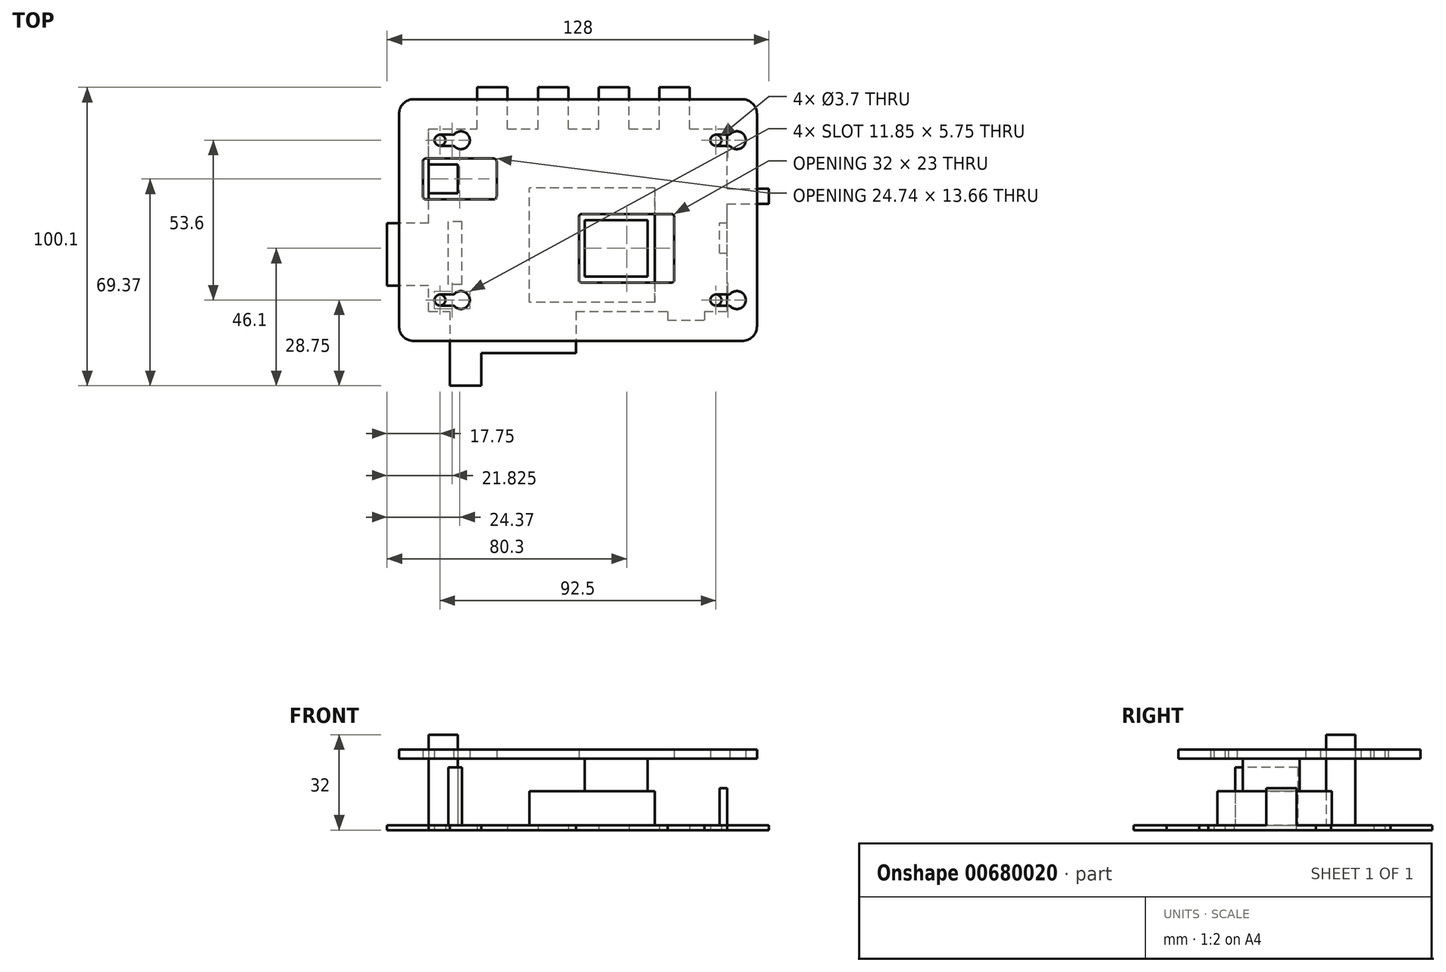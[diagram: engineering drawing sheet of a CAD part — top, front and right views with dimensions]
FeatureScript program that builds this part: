
annotation { "Feature Type Name" : "Feature", "Feature Type Description" : "" }
export const myFeature = defineFeature(function(context is Context, id is Id, definition is map)
    precondition{}
    {
        {
            var Q0;
            Q0=qCreatedBy(makeId("Top.planeOp"),FACE);
            var sketch = newSketch(context, id + "F0", { "sketchPlane" : qUnion([Q0])});
            skLineSegment(sketch, "E0.bottom", {"start": v(0, 0) * mm, "end": v(100, 0) * mm});
            skLineSegment(sketch, "E0.top", {"start": v(0, 61.1) * mm, "end": v(100, 61.1) * mm});
            skLineSegment(sketch, "E0.left", {"start": v(0, 0) * mm, "end": v(0, 61.1) * mm});
            skLineSegment(sketch, "E0.right", {"start": v(100, 0) * mm, "end": v(100, 61.1) * mm});
            skLineSegment(sketch, "E1.bottom", {"start": v(3.75, 3.75) * mm, "end": v(96.25, 3.75) * mm, "construction": true});
            skLineSegment(sketch, "E1.top", {"start": v(3.75, 57.35) * mm, "end": v(96.25, 57.35) * mm, "construction": true});
            skLineSegment(sketch, "E1.left", {"start": v(3.75, 3.75) * mm, "end": v(3.75, 57.35) * mm, "construction": true});
            skLineSegment(sketch, "E1.right", {"start": v(96.25, 3.75) * mm, "end": v(96.25, 57.35) * mm, "construction": true});
            skCircle(sketch, "E2", {"center": v(3.75, 3.75) * mm, "radius": 1.85 * mm});
            skCircle(sketch, "E3", {"center": v(3.75, 57.35) * mm, "radius": 1.85 * mm});
            skCircle(sketch, "E4", {"center": v(96.25, 57.35) * mm, "radius": 1.85 * mm});
            skCircle(sketch, "E5", {"center": v(96.25, 3.75) * mm, "radius": 1.85 * mm});
            skLineSegment(sketch, "E6.bottom", {"start": v(0, 49.2) * mm, "end": v(9.74, 49.2) * mm});
            skLineSegment(sketch, "E6.top", {"start": v(0, 39.54) * mm, "end": v(9.74, 39.54) * mm});
            skLineSegment(sketch, "E6.left", {"start": v(0, 49.2) * mm, "end": v(0, 39.54) * mm});
            skLineSegment(sketch, "E6.right", {"start": v(9.74, 49.2) * mm, "end": v(9.74, 39.54) * mm});
            skLineSegment(sketch, "E7.bottom", {"start": v(6.58, 30) * mm, "end": v(11.08, 30) * mm});
            skLineSegment(sketch, "E7.top", {"start": v(6.58, 9) * mm, "end": v(11.08, 9) * mm});
            skLineSegment(sketch, "E7.left", {"start": v(6.58, 30) * mm, "end": v(6.58, 9) * mm});
            skLineSegment(sketch, "E7.right", {"start": v(11.08, 30) * mm, "end": v(11.08, 9) * mm});
            skLineSegment(sketch, "E8.bottom", {"start": v(7.05, 0) * mm, "end": v(17.55, 0) * mm});
            skLineSegment(sketch, "E8.top", {"start": v(7.05, -25) * mm, "end": v(17.55, -25) * mm});
            skLineSegment(sketch, "E8.left", {"start": v(7.05, 0) * mm, "end": v(7.05, -25) * mm});
            skLineSegment(sketch, "E8.right", {"start": v(17.55, 0) * mm, "end": v(17.55, -25) * mm});
            skLineSegment(sketch, "E9.bottom", {"start": v(17.5, 0) * mm, "end": v(49.3, 0) * mm});
            skLineSegment(sketch, "E9.top", {"start": v(17.5, -14) * mm, "end": v(49.3, -14) * mm});
            skLineSegment(sketch, "E9.left", {"start": v(17.5, 0) * mm, "end": v(17.5, -14) * mm});
            skLineSegment(sketch, "E9.right", {"start": v(49.3, 0) * mm, "end": v(49.3, -14) * mm});
            skLineSegment(sketch, "E10.bottom", {"start": v(80.05, 0) * mm, "end": v(92.35, 0) * mm});
            skLineSegment(sketch, "E10.top", {"start": v(80.05, -3) * mm, "end": v(92.35, -3) * mm});
            skLineSegment(sketch, "E10.left", {"start": v(80.05, 0) * mm, "end": v(80.05, -3) * mm});
            skLineSegment(sketch, "E10.right", {"start": v(92.35, 0) * mm, "end": v(92.35, -3) * mm});
            skLineSegment(sketch, "E11.bottom", {"start": v(16.23, 61.1) * mm, "end": v(26.39, 61.1) * mm});
            skLineSegment(sketch, "E11.top", {"start": v(16.23, 75.1) * mm, "end": v(26.39, 75.1) * mm});
            skLineSegment(sketch, "E11.left", {"start": v(16.23, 61.1) * mm, "end": v(16.23, 75.1) * mm});
            skLineSegment(sketch, "E11.right", {"start": v(26.39, 61.1) * mm, "end": v(26.39, 75.1) * mm});
            skLineSegment(sketch, "E12.bottom", {"start": v(36.59, 61.1) * mm, "end": v(46.75, 61.1) * mm});
            skLineSegment(sketch, "E12.top", {"start": v(36.59, 75.1) * mm, "end": v(46.75, 75.1) * mm});
            skLineSegment(sketch, "E12.left", {"start": v(36.59, 61.1) * mm, "end": v(36.59, 75.1) * mm});
            skLineSegment(sketch, "E12.right", {"start": v(46.75, 61.1) * mm, "end": v(46.75, 75.1) * mm});
            skLineSegment(sketch, "E13.bottom", {"start": v(56.95, 61.1) * mm, "end": v(67.1, 61.1) * mm});
            skLineSegment(sketch, "E13.top", {"start": v(56.95, 75.1) * mm, "end": v(67.1, 75.1) * mm});
            skLineSegment(sketch, "E13.left", {"start": v(56.95, 61.1) * mm, "end": v(56.95, 75.1) * mm});
            skLineSegment(sketch, "E13.right", {"start": v(67.1, 61.1) * mm, "end": v(67.1, 75.1) * mm});
            skLineSegment(sketch, "E14.bottom", {"start": v(77.3, 61.1) * mm, "end": v(87.47, 61.1) * mm});
            skLineSegment(sketch, "E14.top", {"start": v(77.3, 75.1) * mm, "end": v(87.47, 75.1) * mm});
            skLineSegment(sketch, "E14.left", {"start": v(77.3, 61.1) * mm, "end": v(77.3, 75.1) * mm});
            skLineSegment(sketch, "E14.right", {"start": v(87.47, 61.1) * mm, "end": v(87.47, 75.1) * mm});
            skLineSegment(sketch, "E15", {"start": v(26.39, 75.1) * mm, "end": v(36.59, 75.1) * mm, "construction": true});
            skLineSegment(sketch, "E16", {"start": v(46.75, 75.1) * mm, "end": v(56.95, 75.1) * mm, "construction": true});
            skLineSegment(sketch, "E17", {"start": v(67.1, 75.1) * mm, "end": v(77.3, 75.1) * mm, "construction": true});
            skLineSegment(sketch, "E18.bottom", {"start": v(100, 29.6) * mm, "end": v(97.46, 29.6) * mm});
            skLineSegment(sketch, "E18.top", {"start": v(100, 19.44) * mm, "end": v(97.46, 19.44) * mm});
            skLineSegment(sketch, "E18.left", {"start": v(100, 29.6) * mm, "end": v(100, 19.44) * mm});
            skLineSegment(sketch, "E18.right", {"start": v(97.46, 29.6) * mm, "end": v(97.46, 19.44) * mm});
            skLineSegment(sketch, "E19.bottom", {"start": v(100, 41.1) * mm, "end": v(114, 41.1) * mm});
            skLineSegment(sketch, "E19.top", {"start": v(100, 36) * mm, "end": v(114, 36) * mm});
            skLineSegment(sketch, "E19.left", {"start": v(100, 41.1) * mm, "end": v(100, 36) * mm});
            skLineSegment(sketch, "E19.right", {"start": v(114, 41.1) * mm, "end": v(114, 36) * mm});
            skPoint(sketch, "E20", {"position": v(12.3, 0) * mm});
            skLineSegment(sketch, "E21.bottom", {"start": v(0, 29.5) * mm, "end": v(-14, 29.5) * mm});
            skLineSegment(sketch, "E21.top", {"start": v(0, 8.6) * mm, "end": v(-14, 8.6) * mm});
            skLineSegment(sketch, "E21.left", {"start": v(0, 29.5) * mm, "end": v(0, 8.6) * mm});
            skLineSegment(sketch, "E21.right", {"start": v(-14, 29.5) * mm, "end": v(-14, 8.6) * mm});
            skSolve(sketch);
        }
        {
            var Q0;
            Q0=qSketchRegion(id+"F0",true);
            var Q1;
            Q1=makeQuery(id+"F0.imprint","IMPRINT",FACE,{"disambiguationData":[TD([[makeQuery(id+"F0.imprint","IMPRINT",EDGE,{"derivedFrom":sQuery(id+"F0.wireOp",EDGE,"E7.bottom")}),-1.0]])]});
            extrude(context, id + "F1", {"entities" : qUnion([Q0, Q1]), "depth" : 1.6 * mm});
        }
        {
            var Q0;
            Q0=makeQuery(id+"F0.imprint","IMPRINT",FACE,{"disambiguationData":[TD([[makeQuery(id+"F0.imprint","IMPRINT",EDGE,{"derivedFrom":sQuery(id+"F0.wireOp",EDGE,"E6.bottom")}),-1.0]])]});
            extrude(context, id + "F2", {"entities" : qUnion([Q0]), "operationType" : NewBodyOperationType.ADD, "depth" : 32 * mm});
        }
        {
            var Q0;
            Q0=makeQuery(id+"F0.imprint","IMPRINT",FACE,{"disambiguationData":[TD([[makeQuery(id+"F0.imprint","IMPRINT",EDGE,{"derivedFrom":sQuery(id+"F0.wireOp",EDGE,"E7.bottom")}),-1.0]])]});
            extrude(context, id + "F3", {"entities" : qUnion([Q0]), "operationType" : NewBodyOperationType.ADD, "depth" : 21 * mm});
        }
        {
            var Q0;
            Q0=makeQuery(id+"F0.imprint","IMPRINT",FACE,{"disambiguationData":[TD([[makeQuery(id+"F0.imprint","IMPRINT",EDGE,{"derivedFrom":sQuery(id+"F0.wireOp",EDGE,"E18.bottom")}),1.0]])]});
            extrude(context, id + "F4", {"entities" : qUnion([Q0]), "operationType" : NewBodyOperationType.ADD, "depth" : 14 * mm});
        }
        {
            var Q0;
            Q0=qCreatedBy(makeId("Top.planeOp"),FACE);
            var sketch = newSketch(context, id + "F5", { "sketchPlane" : qUnion([Q0])});
            skLineSegment(sketch, "E22.bottom", {"start": v(33.7, 41.4) * mm, "end": v(75.8, 41.4) * mm});
            skLineSegment(sketch, "E22.top", {"start": v(33.7, 3) * mm, "end": v(75.8, 3) * mm});
            skLineSegment(sketch, "E22.left", {"start": v(33.7, 41.4) * mm, "end": v(33.7, 3) * mm});
            skLineSegment(sketch, "E22.right", {"start": v(75.8, 41.4) * mm, "end": v(75.8, 3) * mm});
            skLineSegment(sketch, "E23.bottom", {"start": v(73.3, 30.6) * mm, "end": v(52.3, 30.6) * mm});
            skLineSegment(sketch, "E23.top", {"start": v(73.3, 11.6) * mm, "end": v(52.3, 11.6) * mm});
            skLineSegment(sketch, "E23.left", {"start": v(73.3, 30.6) * mm, "end": v(73.3, 11.6) * mm});
            skLineSegment(sketch, "E23.right", {"start": v(52.3, 30.6) * mm, "end": v(52.3, 11.6) * mm});
            skPoint(sketch, "E23.middle", {"position": v(62.8, 21.1) * mm});
            skSolve(sketch);
        }
        {
            var Q0;
            Q0=makeQuery(id+"F5.imprint","IMPRINT",FACE,{"disambiguationData":[TD([[makeQuery(id+"F5.imprint","IMPRINT",EDGE,{"derivedFrom":sQuery(id+"F5.wireOp",EDGE,"E23.bottom")}),1.0]])]});
            var Q1;
            Q1=makeQuery(id+"F5.imprint","IMPRINT",FACE,{"disambiguationData":[TD([[makeQuery(id+"F5.imprint","IMPRINT",EDGE,{"derivedFrom":sQuery(id+"F5.wireOp",EDGE,"E22.bottom")}),-1.0]])]});
            extrude(context, id + "F6", {"entities" : qUnion([Q0, Q1]), "operationType" : NewBodyOperationType.ADD, "depth" : 13 * mm});
        }
        {
            var Q0;
            Q0=makeQuery(id+"F5.imprint","IMPRINT",FACE,{"disambiguationData":[TD([[makeQuery(id+"F5.imprint","IMPRINT",EDGE,{"derivedFrom":sQuery(id+"F5.wireOp",EDGE,"E23.bottom")}),1.0]])]});
            extrude(context, id + "F7", {"entities" : qUnion([Q0]), "operationType" : NewBodyOperationType.ADD, "depth" : 24 * mm});
        }
        {
            var Q0;
            Q0=makeQuery(id+"F7.opExtrude","CAP_FACE",FACE,{"disambiguationData":[OSD([sQuery(id+"F5.wireOp",EDGE,"E23.bottom"),sQuery(id+"F5.wireOp",EDGE,"E23.top"),sQuery(id+"F5.wireOp",EDGE,"E23.left"),sQuery(id+"F5.wireOp",EDGE,"E23.right")])],"isStart":false});
            var sketch = newSketch(context, id + "F8", { "sketchPlane" : qUnion([Q0])});
            skCircle(sketch, "E24.0", {"center": v(96.25, 57.35) * mm, "radius": 1.85 * mm});
            skCircle(sketch, "E25.0", {"center": v(96.25, 3.75) * mm, "radius": 1.85 * mm});
            skCircle(sketch, "E26.0", {"center": v(3.75, 3.75) * mm, "radius": 1.85 * mm});
            skCircle(sketch, "E27.0", {"center": v(3.75, 57.35) * mm, "radius": 1.85 * mm});
            skPoint(sketch, "E28.0", {"position": v(0, 61.1) * mm});
            skPoint(sketch, "E29.0", {"position": v(100, 61.1) * mm});
            skPoint(sketch, "E30.0", {"position": v(100, 0) * mm});
            skLineSegment(sketch, "E31.0.0", {"start": v(52.3, 11.6) * mm, "end": v(73.3, 11.6) * mm, "construction": true});
            skLineSegment(sketch, "E31.0.1", {"start": v(73.3, 11.6) * mm, "end": v(73.3, 30.6) * mm, "construction": true});
            skLineSegment(sketch, "E31.0.2", {"start": v(73.3, 30.6) * mm, "end": v(52.3, 30.6) * mm, "construction": true});
            skLineSegment(sketch, "E31.0.3", {"start": v(52.3, 30.6) * mm, "end": v(52.3, 11.6) * mm, "construction": true});
            skPoint(sketch, "E32.visualSharp", {"position": v(0, 0) * mm});
            skLineSegment(sketch, "E33.bottom", {"start": v(51.3, 32.6) * mm, "end": v(81.3, 32.6) * mm});
            skLineSegment(sketch, "E33.top", {"start": v(51.3, 9.6) * mm, "end": v(81.3, 9.6) * mm});
            skLineSegment(sketch, "E33.left", {"start": v(50.3, 31.6) * mm, "end": v(50.3, 10.6) * mm});
            skLineSegment(sketch, "E33.right", {"start": v(82.3, 31.6) * mm, "end": v(82.3, 10.6) * mm});
            skPoint(sketch, "E34.visualSharp", {"position": v(50.3, 32.6) * mm});
            skArc(sketch, "E34.filletArc", {"start": v(51.3, 32.6) * mm, "mid": v(50.6, 32.3) * mm, "end": v(50.3, 31.6) * mm});
            skPoint(sketch, "E35.visualSharp", {"position": v(82.3, 32.6) * mm});
            skArc(sketch, "E35.filletArc", {"start": v(82.3, 31.6) * mm, "mid": v(82, 32.3) * mm, "end": v(81.3, 32.6) * mm});
            skPoint(sketch, "E36.visualSharp", {"position": v(82.3, 9.6) * mm});
            skArc(sketch, "E36.filletArc", {"start": v(81.3, 9.6) * mm, "mid": v(82, 9.9) * mm, "end": v(82.3, 10.6) * mm});
            skPoint(sketch, "E37.visualSharp", {"position": v(50.3, 9.6) * mm});
            skArc(sketch, "E37.filletArc", {"start": v(50.3, 10.6) * mm, "mid": v(50.6, 9.9) * mm, "end": v(51.3, 9.6) * mm});
            skLineSegment(sketch, "E38.bottom", {"start": v(-5, 71.1) * mm, "end": v(105, 71.1) * mm});
            skLineSegment(sketch, "E38.top", {"start": v(-5, -10) * mm, "end": v(105, -10) * mm});
            skLineSegment(sketch, "E38.left", {"start": v(-10, 66.1) * mm, "end": v(-10, -5) * mm});
            skLineSegment(sketch, "E38.right", {"start": v(110, 66.1) * mm, "end": v(110, -5) * mm});
            skPoint(sketch, "E39.visualSharp", {"position": v(-10, 71.1) * mm});
            skArc(sketch, "E39.filletArc", {"start": v(-5, 71.1) * mm, "mid": v(-8.54, 69.64) * mm, "end": v(-10, 66.1) * mm});
            skPoint(sketch, "E40.visualSharp", {"position": v(110, 71.1) * mm});
            skArc(sketch, "E40.filletArc", {"start": v(110, 66.1) * mm, "mid": v(108.54, 69.64) * mm, "end": v(105, 71.1) * mm});
            skPoint(sketch, "E41.visualSharp", {"position": v(110, -10) * mm});
            skArc(sketch, "E41.filletArc", {"start": v(105, -10) * mm, "mid": v(108.54, -8.54) * mm, "end": v(110, -5) * mm});
            skPoint(sketch, "E42.visualSharp", {"position": v(-10, -10) * mm});
            skArc(sketch, "E42.filletArc", {"start": v(-10, -5) * mm, "mid": v(-8.54, -8.54) * mm, "end": v(-5, -10) * mm});
            skLineSegment(sketch, "E43.0.0", {"start": v(9.74, 49.2) * mm, "end": v(0, 49.2) * mm, "construction": true});
            skLineSegment(sketch, "E43.0.1", {"start": v(0, 49.2) * mm, "end": v(0, 39.54) * mm, "construction": true});
            skLineSegment(sketch, "E43.0.2", {"start": v(0, 39.54) * mm, "end": v(9.74, 39.54) * mm, "construction": true});
            skLineSegment(sketch, "E43.0.3", {"start": v(9.74, 39.54) * mm, "end": v(9.74, 49.2) * mm, "construction": true});
            skLineSegment(sketch, "E44.bottom", {"start": v(-1, 37.54) * mm, "end": v(21.74, 37.54) * mm});
            skLineSegment(sketch, "E44.top", {"start": v(-1, 51.2) * mm, "end": v(21.74, 51.2) * mm});
            skLineSegment(sketch, "E44.left", {"start": v(-2, 38.54) * mm, "end": v(-2, 50.2) * mm});
            skLineSegment(sketch, "E44.right", {"start": v(22.74, 38.54) * mm, "end": v(22.74, 50.2) * mm});
            skLineSegment(sketch, "E45", {"start": v(3.75, 3.75) * mm, "end": v(10.75, 3.75) * mm, "construction": true});
            skCircle(sketch, "E46", {"center": v(10.75, 3.75) * mm, "radius": 3 * mm});
            skLineSegment(sketch, "E47", {"start": v(3.75, 57.35) * mm, "end": v(10.75, 57.35) * mm, "construction": true});
            skCircle(sketch, "E48", {"center": v(10.75, 57.35) * mm, "radius": 3 * mm});
            skLineSegment(sketch, "E49", {"start": v(3.75, 5.6) * mm, "end": v(8.39, 5.6) * mm});
            skLineSegment(sketch, "E50", {"start": v(3.75, 1.9) * mm, "end": v(8.39, 1.9) * mm});
            skLineSegment(sketch, "E51", {"start": v(96.25, 3.75) * mm, "end": v(103.25, 3.75) * mm, "construction": true});
            skCircle(sketch, "E52", {"center": v(103.25, 3.75) * mm, "radius": 3 * mm});
            skLineSegment(sketch, "E53", {"start": v(96.25, 5.6) * mm, "end": v(100.89, 5.6) * mm});
            skLineSegment(sketch, "E54", {"start": v(96.25, 1.9) * mm, "end": v(100.89, 1.9) * mm});
            skPoint(sketch, "E55.visualSharp", {"position": v(-2, 51.2) * mm});
            skArc(sketch, "E55.filletArc", {"start": v(-1, 51.2) * mm, "mid": v(-1.7, 50.9) * mm, "end": v(-2, 50.2) * mm});
            skPoint(sketch, "E56.visualSharp", {"position": v(-2, 37.54) * mm});
            skArc(sketch, "E56.filletArc", {"start": v(-2, 38.54) * mm, "mid": v(-1.7, 37.83) * mm, "end": v(-1, 37.54) * mm});
            skPoint(sketch, "E57.visualSharp", {"position": v(22.74, 37.54) * mm});
            skArc(sketch, "E57.filletArc", {"start": v(21.74, 37.54) * mm, "mid": v(22.45, 37.83) * mm, "end": v(22.74, 38.54) * mm});
            skPoint(sketch, "E58.visualSharp", {"position": v(22.74, 51.2) * mm});
            skArc(sketch, "E58.filletArc", {"start": v(22.74, 50.2) * mm, "mid": v(22.45, 50.9) * mm, "end": v(21.74, 51.2) * mm});
            skLineSegment(sketch, "E59", {"start": v(96.25, 57.35) * mm, "end": v(103.25, 57.35) * mm, "construction": true});
            skCircle(sketch, "E60", {"center": v(103.25, 57.35) * mm, "radius": 3 * mm});
            skLineSegment(sketch, "E61", {"start": v(96.25, 55.5) * mm, "end": v(100.89, 55.5) * mm});
            skLineSegment(sketch, "E62", {"start": v(96.25, 59.2) * mm, "end": v(100.89, 59.2) * mm});
            skLineSegment(sketch, "E63", {"start": v(3.75, 59.2) * mm, "end": v(8.39, 59.2) * mm});
            skLineSegment(sketch, "E64", {"start": v(3.75, 55.5) * mm, "end": v(8.39, 55.5) * mm});
            skSolve(sketch);
        }
        {
            var Q0;
            Q0=makeQuery(id+"F8.imprint","IMPRINT",FACE,{"disambiguationData":[TD([[makeQuery(id+"F8.imprint","IMPRINT",EDGE,{"derivedFrom":sQuery(id+"F8.wireOp",EDGE,"E33.bottom")}),1.0]])]});
            extrude(context, id + "F9", {"entities" : qUnion([Q0]), "depth" : 3 * mm});
        }
    });
